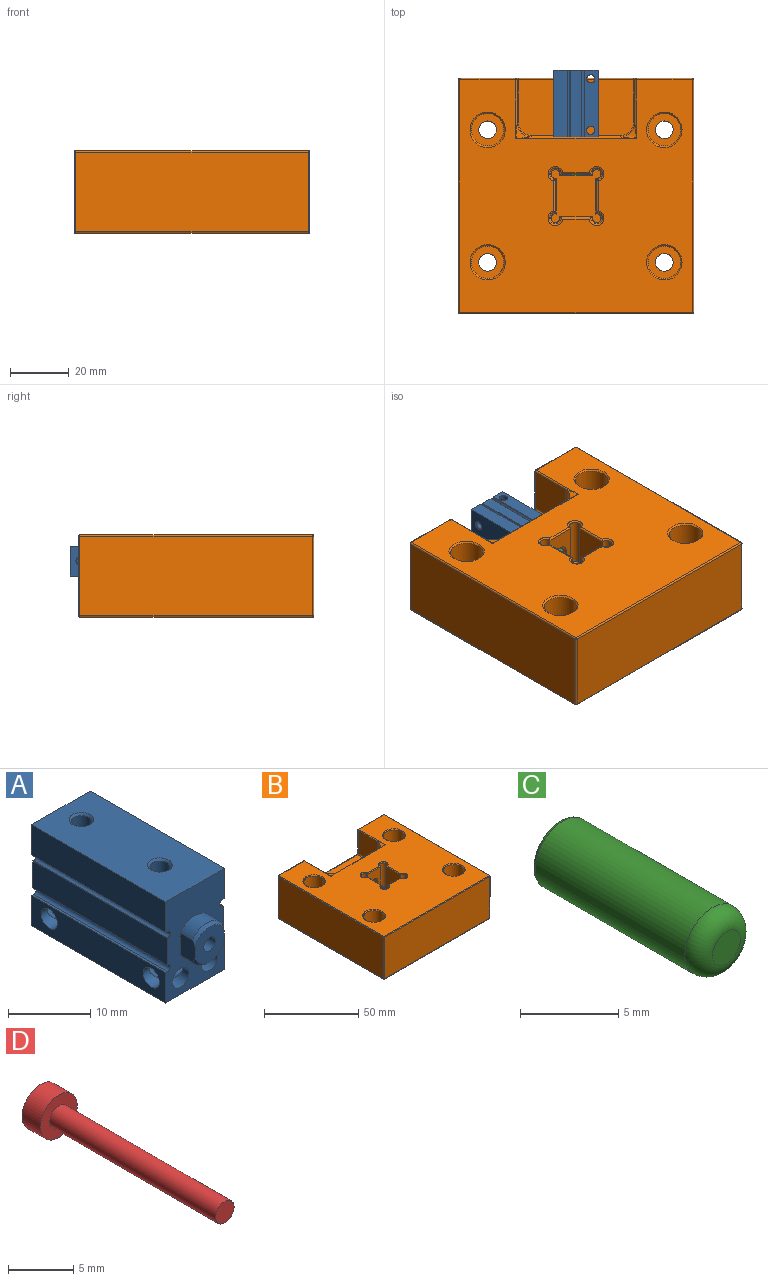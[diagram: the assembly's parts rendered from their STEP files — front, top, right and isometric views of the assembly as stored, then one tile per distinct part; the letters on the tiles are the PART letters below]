
ASSEMBLY  parts=4 mates=3
PART A: 51 faces, bbox 10.1x25.6x15.1 mm
  f0: cone r=1.23mm half-angle=60deg, axis (0,0,1), area 5.5mm2, adj f47
  f1: plane 3.43x2.62mm, normal (-1,0,0), area 8mm2, adj f2,f5,f6,f7,f8,f9
  f2: cylinder r=3mm len=5mm, axis (0,-1,0), area 12.4mm2, adj f1,f6,f9,f42
  f3: plane 4x4mm, normal (0,1,0), area 9.4mm2, adj f4,f40
  f4: cylinder r=1mm len=5mm, axis (0,-1,0), area 31.4mm2, adj f3,f5
  f5: plane 5.2x5mm, normal (0,-1,0), area 17.9mm2, adj f1,f4,f6,f7,f42
  f6: cone r=3mm half-angle=45deg, axis (0,1,0), area 3.6mm2, adj f1,f2,f5,f42
  f7: cone r=3mm half-angle=45deg, axis (0,1,0), area 3.6mm2, adj f1,f5,f8,f42
  f8: cylinder r=3mm len=5mm, axis (0,-1,0), area 12.4mm2, adj f1,f7,f9,f42
  f9: plane 15x10mm, normal (0,-1,0), area 107.3mm2, adj f1,f2,f8,f14,f15,f16,f17,f18
  f10: cylinder r=1.4mm len=5mm, axis (1,0,0), area 29.1mm2, adj f34,f35,f36,f49
  f11: plane 15x10mm, normal (0,1,0), area 133.3mm2, adj f12,f13,f14,f15,f16,f17,f18,f19
  f12: cylinder r=1.4mm len=3mm, axis (0,1,0), area 19.4mm2, adj f11,f37,f38
  f13: cylinder r=1.4mm len=3mm, axis (0,1,0), area 19.4mm2, adj f11,f38,f39
  f14: plane 23x10mm, normal (0,0,1), area 215.9mm2, adj f9,f11,f15,f33,f43,f46
  f15: plane 23x4.5mm, normal (1,0,0), area 103.5mm2, adj f9,f11,f14,f16
  f16: plane 23x0.3mm, normal (0,0,-1), area 6.9mm2, adj f9,f11,f15,f17
  f17: cylinder r=0.5mm len=23mm, axis (0,1,0), area 36.1mm2, adj f9,f11,f16,f18
  f18: plane 23x0.1mm, normal (0,0,1), area 2.3mm2, adj f9,f11,f17,f19
  f19: plane 23x4mm, normal (1,0,0), area 92mm2, adj f9,f11,f18,f20
  f20: plane 23x0.1mm, normal (0,0,-1), area 2.3mm2, adj f9,f11,f19,f21
  f21: cylinder r=0.5mm len=23mm, axis (0,1,0), area 36.1mm2, adj f9,f11,f20,f22
  f22: plane 23x0.3mm, normal (0,0,1), area 6.9mm2, adj f9,f11,f21,f23
  f23: plane 23x4.5mm, normal (1,0,0), area 91.2mm2, adj f9,f11,f22,f24,f39,f50
  f24: plane 23x10mm, normal (0,0,-1), area 230mm2, adj f9,f11,f23,f25
  f25: plane 23x4.5mm, normal (-1,0,0), area 91.2mm2, adj f9,f11,f24,f26,f37,f48
  f26: plane 23x0.3mm, normal (0,0,1), area 6.9mm2, adj f9,f11,f25,f27
  f27: cylinder r=0.5mm len=23mm, axis (0,1,0), area 36.1mm2, adj f9,f11,f26,f28
  f28: plane 23x0.1mm, normal (0,0,-1), area 2.3mm2, adj f9,f11,f27,f29
  f29: plane 23x4mm, normal (-1,0,0), area 92mm2, adj f9,f11,f28,f30
  f30: plane 23x0.1mm, normal (0,0,1), area 2.3mm2, adj f9,f11,f29,f31
  f31: cylinder r=0.5mm len=23mm, axis (0,1,0), area 36.1mm2, adj f9,f11,f30,f32
  f32: plane 23x0.3mm, normal (0,0,-1), area 6.9mm2, adj f9,f11,f31,f33
  f33: plane 23x4.5mm, normal (-1,0,0), area 103.5mm2, adj f9,f11,f14,f32
  f34: cylinder r=1.4mm len=2.8mm, axis (0,1,0), area 15.8mm2, adj f9,f10,f48
  f35: cylinder r=1.4mm len=2.8mm, axis (0,1,0), area 15mm2, adj f9,f10,f50
  f36: cylinder r=1.4mm len=17.5mm, axis (0,1,0), area 139.1mm2, adj f10,f37,f38,f48
  f37: cylinder r=1.4mm len=2.8mm, axis (1,0,0), area 15mm2, adj f12,f25,f36
  f38: cylinder r=1.4mm len=5mm, axis (1,0,0), area 29.1mm2, adj f12,f13,f36,f49
  f39: cylinder r=1.4mm len=2.8mm, axis (1,0,0), area 15mm2, adj f13,f23,f49
  f40: cylinder r=2mm len=12mm, axis (0,-1,0), area 150.8mm2, adj f3,f41
  f41: plane 4x4mm, normal (0,-1,0), area 12.6mm2, adj f40
  f42: plane 3.43x2.62mm, normal (1,0,0), area 8mm2, adj f2,f5,f6,f7,f8,f9
  f43: cone r=1.5mm half-angle=45deg, axis (0,0,1), area 3.3mm2, adj f14,f44
  f44: cylinder r=1.23mm len=3.23mm, axis (0,0,1), area 24.9mm2, adj f43,f45
  f45: cone r=1.23mm half-angle=60deg, axis (0,0,1), area 5.5mm2, adj f44
  f46: cone r=1.5mm half-angle=45deg, axis (0,0,1), area 3.3mm2, adj f14,f47
  f47: cylinder r=1.23mm len=3.23mm, axis (0,0,1), area 24.9mm2, adj f0,f46
  f48: cylinder r=1.4mm len=2.8mm, axis (1,0,0), area 15mm2, adj f25,f34,f36
  f49: cylinder r=1.4mm len=17.5mm, axis (0,1,0), area 138.3mm2, adj f10,f38,f39,f50
  f50: cylinder r=1.4mm len=2.8mm, axis (1,0,0), area 15mm2, adj f23,f35,f49
PART B: 105 faces, bbox 80x80x28 mm
  f0: bspline ~5.43x5.43mm, area 8.6mm2, adj f46,f53,f95,f96
  f1: bspline ~5.43x5.43mm, area 8.6mm2, adj f53,f57,f98,f99
  f2: plane 39x19mm, normal (0,0,1), area 732.3mm2, adj f32,f41,f47,f48,f97,f100
  f3: cylinder r=3mm len=19.5mm, axis (0,0,1), area 367.6mm2, adj f67,f93
  f4: cylinder r=3mm len=19.5mm, axis (0,0,1), area 367.6mm2, adj f66,f91
  f5: cylinder r=3mm len=19.5mm, axis (0,0,1), area 367.6mm2, adj f65,f89
  f6: cylinder r=3mm len=19.5mm, axis (0,0,1), area 367.6mm2, adj f64,f87
  f7: plane 79x27mm, normal (0,1,0), area 1477.4mm2, adj f33,f34,f35,f42,f48,f49,f54,f58
  f8: plane 79x79mm, normal (0,0,1), area 4680.6mm2, adj f33,f39,f46,f52,f53,f57,f60,f63
  f9: plane 79x27mm, normal (-1,0,0), area 2133mm2, adj f35,f36,f38,f39
  f10: plane 79x27mm, normal (0,-1,0), area 2133mm2, adj f37,f38,f51,f52
  f11: plane 79x27mm, normal (1,0,0), area 2133mm2, adj f50,f51,f59,f60
  f12: plane 79x79mm, normal (0,0,-1), area 6087.1mm2, adj f36,f37,f49,f50,f64,f65,f66,f67
  f13: plane 16x10mm, normal (0,-1,0), area 131.7mm2, adj f14,f20,f25,f72,f80
  f14: cylinder r=2mm len=16mm, axis (0,0,1), area 150.8mm2, adj f13,f15,f70,f78
  f15: plane 16x11mm, normal (1,0,0), area 176mm2, adj f14,f16,f68,f76
  f16: cylinder r=2mm len=16mm, axis (0,0,1), area 150.8mm2, adj f15,f17,f69,f77
  f17: plane 16x10mm, normal (0,1,0), area 160mm2, adj f16,f18,f71,f79
  f18: cylinder r=2mm len=16mm, axis (0,0,1), area 150.8mm2, adj f17,f19,f73,f81
  f19: plane 16x11mm, normal (-1,0,0), area 176mm2, adj f18,f20,f75,f83
  f20: cylinder r=2mm len=16mm, axis (0,0,1), area 150.8mm2, adj f13,f19,f74,f82
  f21: plane 18x17mm, normal (0,0,1), area 208.1mm2, adj f76,f77,f78,f79,f80,f81,f82,f83
  f22: plane 15x14.5mm, normal (1,0,0), area 217.5mm2, adj f32,f34,f46,f96
  f23: plane 30x15mm, normal (0,1,0), area 404.6mm2, adj f41,f53,f84,f85,f86,f96,f99
  f24: plane 15x14.5mm, normal (-1,0,0), area 217.5mm2, adj f47,f57,f58,f99
  f25: cylinder r=3mm len=12.3mm, axis (0,1,0), area 231.8mm2, adj f13,f86
  f26: cylinder r=1.25mm len=4.8mm, axis (0,1,0), area 37.7mm2, adj f27,f85
  f27: plane 2.5x2.5mm, normal (0,1,0), area 4.9mm2, adj f26
  f28: cylinder r=1.25mm len=4.8mm, axis (0,1,0), area 37.7mm2, adj f29,f84
  f29: plane 2.5x2.5mm, normal (0,1,0), area 4.9mm2, adj f28
  f30: sphere r=0.5mm, area 0.4mm2, adj f36,f37,f38
  f31: sphere r=0.5mm, area 0.5mm2, adj f33,f35,f39
  f32: cylinder r=0.5mm len=14.5mm, axis (0,-1,0), area 11.4mm2, adj f2,f22,f42,f97
  f33: cylinder r=0.5mm len=19mm, axis (1,0,0), area 14.9mm2, adj f7,f8,f31,f40
  f34: cylinder r=0.5mm len=15mm, axis (0,0,-1), area 11.8mm2, adj f7,f22,f40,f42
  f35: cylinder r=0.5mm len=27mm, axis (0,0,-1), area 21.2mm2, adj f7,f9,f31,f43
  f36: cylinder r=0.5mm len=79mm, axis (0,-1,0), area 62mm2, adj f9,f12,f30,f43
  f37: cylinder r=0.5mm len=79mm, axis (1,0,0), area 62mm2, adj f10,f12,f30,f44
  f38: cylinder r=0.5mm len=27mm, axis (0,0,1), area 21.2mm2, adj f9,f10,f30,f45
  f39: cylinder r=0.5mm len=79mm, axis (0,1,0), area 62mm2, adj f8,f9,f31,f45
  f40: sphere r=0.5mm, area 0.2mm2, adj f33,f34,f46
  f41: cylinder r=0.5mm len=30mm, axis (1,0,0), area 23.6mm2, adj f2,f23,f97,f100
  f42: torus R=1mm, axis (0,1,0), area 0.8mm2, adj f7,f32,f34,f48
  f43: sphere r=0.5mm, area 0.5mm2, adj f35,f36,f49
  f44: sphere r=0.5mm, area 0.4mm2, adj f37,f50,f51
  f45: sphere r=0.5mm, area 0.2mm2, adj f38,f39,f52
  f46: cylinder r=0.5mm len=20mm, axis (0,1,0), area 13mm2, adj f0,f8,f22,f40,f95
  f47: cylinder r=0.5mm len=14.5mm, axis (0,1,0), area 11.4mm2, adj f2,f24,f54,f100
  f48: cylinder r=0.5mm len=39mm, axis (1,0,0), area 30.6mm2, adj f2,f7,f42,f54
  f49: cylinder r=0.5mm len=79mm, axis (-1,0,0), area 62mm2, adj f7,f12,f43,f55
  f50: cylinder r=0.5mm len=79mm, axis (0,1,0), area 62mm2, adj f11,f12,f44,f55
  f51: cylinder r=0.5mm len=27mm, axis (0,0,-1), area 21.2mm2, adj f10,f11,f44,f56
  f52: cylinder r=0.5mm len=79mm, axis (-1,0,0), area 62mm2, adj f8,f10,f45,f56
  f53: cylinder r=0.5mm len=41mm, axis (-1,0,0), area 26.7mm2, adj f0,f1,f8,f23,f95,f98
  f54: torus R=1mm, axis (0,1,0), area 0.8mm2, adj f7,f47,f48,f58
  f55: sphere r=0.5mm, area 0.3mm2, adj f49,f50,f59
  f56: sphere r=0.5mm, area 0.4mm2, adj f51,f52,f60
  f57: cylinder r=0.5mm len=20mm, axis (0,-1,0), area 13mm2, adj f1,f8,f24,f61,f98
  f58: cylinder r=0.5mm len=15mm, axis (0,0,1), area 11.8mm2, adj f7,f24,f54,f61
  f59: cylinder r=0.5mm len=27mm, axis (0,0,1), area 21.2mm2, adj f7,f11,f55,f62
  f60: cylinder r=0.5mm len=79mm, axis (0,-1,0), area 62mm2, adj f8,f11,f56,f62
  f61: sphere r=0.5mm, area 0.5mm2, adj f57,f58,f63
  f62: sphere r=0.5mm, area 0.2mm2, adj f59,f60,f63
  f63: cylinder r=0.5mm len=19mm, axis (1,0,0), area 14.9mm2, adj f7,f8,f61,f62
  f64: torus R=3.5mm, axis (0,0,1), area 15.7mm2, adj f6,f12
  f65: torus R=3.5mm, axis (0,0,1), area 15.7mm2, adj f5,f12
  f66: torus R=3.5mm, axis (0,0,1), area 15.7mm2, adj f4,f12
  f67: torus R=3.5mm, axis (0,0,1), area 15.7mm2, adj f3,f12
  f68: cylinder r=0.5mm len=11mm, axis (0,1,0), area 8.3mm2, adj f8,f15,f69,f70
  f69: torus R=2.5mm, axis (0,0,1), area 7.7mm2, adj f8,f16,f68,f71
  f70: torus R=2.5mm, axis (0,0,1), area 7.7mm2, adj f8,f14,f68,f72
  f71: cylinder r=0.5mm len=10mm, axis (-1,0,0), area 7.5mm2, adj f8,f17,f69,f73
  f72: cylinder r=0.5mm len=10mm, axis (1,0,0), area 7.5mm2, adj f8,f13,f70,f74
  f73: torus R=2.5mm, axis (0,0,1), area 7.7mm2, adj f8,f18,f71,f75
  f74: torus R=2.5mm, axis (0,0,1), area 7.7mm2, adj f8,f20,f72,f75
  f75: cylinder r=0.5mm len=11mm, axis (0,-1,0), area 8.3mm2, adj f8,f19,f73,f74
  f76: cylinder r=0.5mm len=12.17mm, axis (0,-1,0), area 9.1mm2, adj f15,f21,f77,f78
  f77: torus R=1.5mm, axis (0,0,1), area 7.2mm2, adj f16,f21,f76,f79
  f78: torus R=1.5mm, axis (0,0,1), area 7.2mm2, adj f14,f21,f76,f80
  f79: cylinder r=0.5mm len=11.17mm, axis (1,0,0), area 8.3mm2, adj f17,f21,f77,f81
  f80: cylinder r=0.5mm len=11.17mm, axis (-1,0,0), area 8.3mm2, adj f13,f21,f78,f82
  f81: torus R=1.5mm, axis (0,0,1), area 7.2mm2, adj f18,f21,f79,f83
  f82: torus R=1.5mm, axis (0,0,1), area 7.2mm2, adj f20,f21,f80,f83
  f83: cylinder r=0.5mm len=12.17mm, axis (0,1,0), area 9.1mm2, adj f19,f21,f81,f82
  f84: cone r=1.25mm half-angle=45deg, axis (0,1,0), area 2.4mm2, adj f23,f28
  f85: cone r=1.25mm half-angle=45deg, axis (0,1,0), area 2.4mm2, adj f23,f26
  f86: cone r=3mm half-angle=45deg, axis (0,1,0), area 5.5mm2, adj f23,f25
  f87: plane 11x11mm, normal (0,0,1), area 66.8mm2, adj f6,f88
  f88: cylinder r=5.5mm len=11mm, axis (0,0,1), area 259.2mm2, adj f87,f101
  f89: plane 11x11mm, normal (0,0,1), area 66.8mm2, adj f5,f90
  f90: cylinder r=5.5mm len=11mm, axis (0,0,1), area 259.2mm2, adj f89,f103
  f91: plane 11x11mm, normal (0,0,1), area 66.8mm2, adj f4,f92
  f92: cylinder r=5.5mm len=11mm, axis (0,0,1), area 259.2mm2, adj f91,f102
  f93: plane 11x11mm, normal (0,0,1), area 66.8mm2, adj f3,f94
  f94: cylinder r=5.5mm len=11mm, axis (0,0,1), area 259.2mm2, adj f93,f104
  f95: bspline ~1.25x1.25mm, area 0.2mm2, adj f0,f46,f53
  f96: cylinder r=5mm len=15mm, axis (0,0,1), area 117.8mm2, adj f0,f22,f23,f97
  f97: torus R=4.5mm, axis (0,0,1), area 5.9mm2, adj f2,f32,f41,f96
  f98: bspline ~1.25x1.25mm, area 0.2mm2, adj f1,f53,f57
  f99: cylinder r=5mm len=15mm, axis (0,0,-1), area 117.8mm2, adj f1,f23,f24,f100
  f100: torus R=4.5mm, axis (0,0,1), area 5.9mm2, adj f2,f41,f47,f99
  f101: cone r=5.5mm half-angle=45deg, axis (0,0,1), area 25.5mm2, adj f8,f88
  f102: cone r=5.5mm half-angle=45deg, axis (0,0,1), area 25.5mm2, adj f8,f92
  f103: cone r=5.5mm half-angle=45deg, axis (0,0,1), area 25.5mm2, adj f8,f90
  f104: cone r=5.5mm half-angle=45deg, axis (0,0,1), area 25.5mm2, adj f8,f94
PART C: 7 faces, bbox 4.3x12x4.3 mm
  f0: cylinder r=2mm len=10.8mm, axis (0,1,0), area 135.7mm2, adj f3,f4
  f1: plane 2x2mm, normal (0,-1,0), area 3.1mm2, adj f3
  f2: plane 3.6x3.6mm, normal (0,1,0), area 5.3mm2, adj f4,f5
  f3: torus R=1mm, axis (0,-1,0), area 16.2mm2, adj f0,f1
  f4: torus R=1.8mm, axis (0,-1,0), area 3.8mm2, adj f0,f2
  f5: cylinder r=1.25mm len=10mm, axis (0,1,0), area 78.5mm2, adj f2,f6
  f6: plane 2.5x2.5mm, normal (0,1,0), area 4.9mm2, adj f5
PART D: 5 faces, bbox 4x20x4 mm
  f0: cylinder r=2mm len=4mm, axis (0,-1,0), area 25.1mm2, adj f1,f4
  f1: plane 4x4mm, normal (0,-1,0), area 9.4mm2, adj f0,f2
  f2: cylinder r=1mm len=18mm, axis (0,-1,0), area 113.1mm2, adj f1,f3
  f3: plane 2x2mm, normal (0,-1,0), area 3.1mm2, adj f2
  f4: plane 4x4mm, normal (0,1,0), area 12.6mm2, adj f0
PLACE A rot(axis=(0,-1,0),90deg) t=(34.69,54.01,26.28)mm
PLACE B t=(-5.31,-5.79,7.28)mm fixed
PLACE C t=(34.69,53.51,26.28)mm
PLACE D rot(axis=(0,-1,0),90deg) t=(34.69,54.01,26.28)mm
MATE slider D.f0 <-> A.f2  axis (0,1,0) through (34.69,68.51,26.28)mm
MATE fastened A.f13 <-> B.f26  axis (0,-1,0) through (39.69,54.01,28.78)mm
MATE fastened C.f5 <-> D.f0  axis (0,1,0) through (34.69,53.51,26.28)mm
